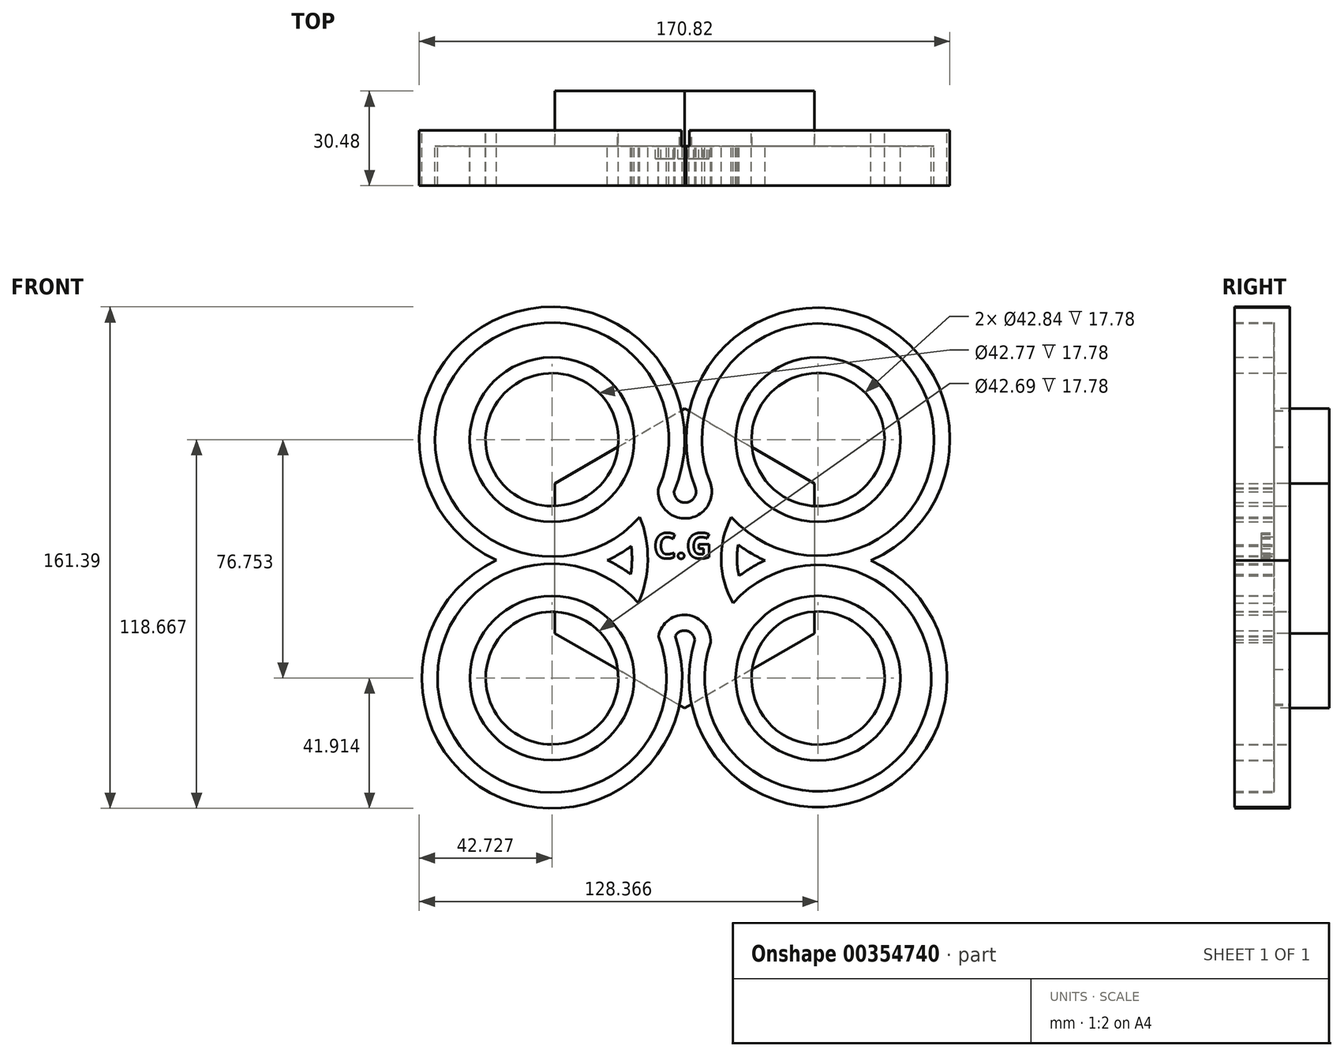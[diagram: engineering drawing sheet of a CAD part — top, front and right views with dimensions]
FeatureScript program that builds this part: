
annotation { "Feature Type Name" : "Feature", "Feature Type Description" : "" }
export const myFeature = defineFeature(function(context is Context, id is Id, definition is map)
    precondition{}
    {
        {
            var Q0;
            Q0=qCreatedBy(makeId("Front.planeOp"),FACE);
            var sketch = newSketch(context, id + "F0", { "sketchPlane" : qUnion([Q0])});
            skCircle(sketch, "E0", {"center": v(-42.72, 38.2) * mm, "radius": 37.65 * mm});
            skCircle(sketch, "E1", {"center": v(42.92, 38.2) * mm, "radius": 37.38 * mm});
            skCircle(sketch, "E2", {"center": v(42.92, -38.55) * mm, "radius": 36.46 * mm});
            skCircle(sketch, "E3", {"center": v(-42.72, -38.55) * mm, "radius": 36.84 * mm});
            skCircle(sketch, "E4", {"center": v(-42.72, 38.2) * mm, "radius": 26.46 * mm});
            skCircle(sketch, "E5", {"center": v(42.92, 38.2) * mm, "radius": 26.5 * mm});
            skCircle(sketch, "E6", {"center": v(42.92, -38.55) * mm, "radius": 26.5 * mm});
            skCircle(sketch, "E7", {"center": v(-42.72, -38.55) * mm, "radius": 26.42 * mm});
            skArc(sketch, "E8", {"start": v(-8.4, 22.72) * mm, "mid": v(0.8, 12.87) * mm, "end": v(8.31, 24.08) * mm});
            skArc(sketch, "E9", {"start": v(8.31, -27.05) * mm, "mid": v(0.85, -18.22) * mm, "end": v(-8.4, -25.14) * mm});
            skArc(sketch, "E10", {"start": v(15, 13.35) * mm, "mid": v(11.74, -0.6) * mm, "end": v(15.59, -14.4) * mm});
            skArc(sketch, "E11", {"start": v(-14.9, -14.4) * mm, "mid": v(-11.9, -0.58) * mm, "end": v(-14.45, 13.35) * mm});
            skSolve(sketch);
        }
        {
            var Q0;
            Q0=qSketchRegion(id+"F0",true);
            extrude(context, id + "F1", {"entities" : qUnion([Q0]), "depth" : 12.7 * mm});
        }
        {
            var Q0;
            Q0=qSketchRegion(id+"F0",true);
            extrude(context, id + "F2", {"entities" : qUnion([Q0]), "operationType" : NewBodyOperationType.ADD, "depth" : 7.87 * mm});
        }
        {
            var Q0;
            Q0=makeQuery(id+"F1.opExtrude","CAP_FACE",FACE,{"disambiguationData":[OSD([sQuery(id+"F0.wireOp",EDGE,"E0"),sQuery(id+"F0.wireOp",EDGE,"E1"),sQuery(id+"F0.wireOp",EDGE,"E2"),sQuery(id+"F0.wireOp",EDGE,"E3"),sQuery(id+"F0.wireOp",EDGE,"E4"),sQuery(id+"F0.wireOp",EDGE,"E5"),sQuery(id+"F0.wireOp",EDGE,"E6"),sQuery(id+"F0.wireOp",EDGE,"E7"),sQuery(id+"F0.wireOp",EDGE,"E8"),sQuery(id+"F0.wireOp",EDGE,"E9"),sQuery(id+"F0.wireOp",EDGE,"E10"),sQuery(id+"F0.wireOp",EDGE,"E11")])],"isStart":false});
            var Q1;
            Q1=makeQuery(id+"F1.opExtrude","SWEPT_BODY",BODY,{"disambiguationData":[OSD([sQuery(id+"F0.wireOp",EDGE,"E0"),sQuery(id+"F0.wireOp",EDGE,"E1"),sQuery(id+"F0.wireOp",EDGE,"E2"),sQuery(id+"F0.wireOp",EDGE,"E3"),sQuery(id+"F0.wireOp",EDGE,"E4"),sQuery(id+"F0.wireOp",EDGE,"E5"),sQuery(id+"F0.wireOp",EDGE,"E6"),sQuery(id+"F0.wireOp",EDGE,"E7"),sQuery(id+"F0.wireOp",EDGE,"E8"),sQuery(id+"F0.wireOp",EDGE,"E9"),sQuery(id+"F0.wireOp",EDGE,"E10"),sQuery(id+"F0.wireOp",EDGE,"E11")])]});
            shell(context, id + "F3", {"entities" : qUnion([Q0]), "parts" : qUnion([Q1]), "thickness" : 5.08 * mm, "oppositeDirection" : true});
        }
        {
            var Q0;
            Q0=qCreatedBy(makeId("Front.planeOp"),FACE);
            var sketch = newSketch(context, id + "F4", { "sketchPlane" : qUnion([Q0])});
            skText(sketch, "E12", { "text": "C.G", "fontName": "OpenSans-Bold.ttf"});
            const initialGuessF4  = {"E12": [-0.01007, 0, 1, 0, 0.00822]};
            skSetInitialGuess(sketch, initialGuessF4);
            skSolve(sketch);
        }
        {
            var Q0;
            Q0=qSketchRegion(id+"F4",true);
            extrude(context, id + "F5", {"entities" : qUnion([Q0]), "operationType" : NewBodyOperationType.ADD, "depth" : 4.06 * mm});
        }
        {
            var Q0;
            Q0=qCreatedBy(makeId("Front.planeOp"),FACE);
            var sketch = newSketch(context, id + "F6", { "sketchPlane" : qUnion([Q0])});
            skCircle(sketch, "E13.cCircle", {"center": v(0, 0) * mm, "radius": 41.78 * mm, "construction": true});
            skLineSegment(sketch, "E13.0", {"start": v(-41.78, -24.12) * mm, "end": v(-41.78, 24.12) * mm});
            skLineSegment(sketch, "E13.1", {"start": v(-41.78, 24.12) * mm, "end": v(0, 48.24) * mm});
            skLineSegment(sketch, "E13.2", {"start": v(0, 48.24) * mm, "end": v(41.78, 24.12) * mm});
            skLineSegment(sketch, "E13.3", {"start": v(41.78, 24.12) * mm, "end": v(41.78, -24.12) * mm});
            skLineSegment(sketch, "E13.4", {"start": v(41.78, -24.12) * mm, "end": v(0, -48.24) * mm});
            skLineSegment(sketch, "E13.5", {"start": v(0, -48.24) * mm, "end": v(-41.78, -24.12) * mm});
            skPoint(sketch, "E13.0.midPoint", {"position": v(-41.78, 0) * mm});
            skSolve(sketch);
        }
        {
            var Q0;
            Q0=qSketchRegion(id+"F6",true);
            extrude(context, id + "F7", {"entities" : qUnion([Q0]), "operationType" : NewBodyOperationType.ADD, "oppositeDirection" : true, "depth" : 17.78 * mm});
        }
    });
